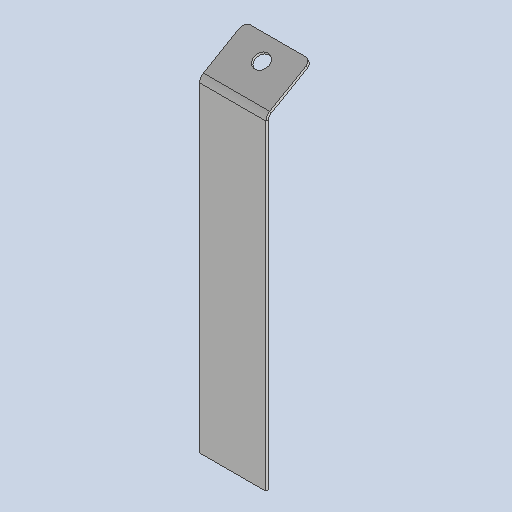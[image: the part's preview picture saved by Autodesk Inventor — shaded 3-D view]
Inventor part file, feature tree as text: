
AUTODESK INVENTOR PART (.ipt)
format: ipt  version: 2025 (Build 290162010, 162A)  size: 308,736 bytes
history: native  units: mm
features: sheet_metal_op x4, other x4, sketch x3, chamfer x1
ambient origin geometry x8: Origin, YZ Plane, XZ Plane, XY Plane, X Axis, Y Axis, Z Axis, Center Point
bodies: Solid1 (feature_tree)
feature tree (12):
  sheet_metal_op  "Face1"
  sheet_metal_op  "Flange1"
  chamfer  "Corner Round1"
  sketch  "Sketch1"  dims[d6=3.0mm]
  other  "Plate1"
  sketch  "Sketch2"  dims[d7=70.0mm]
  other  "Plate2"
  sheet_metal_op  "Bend1"
  sheet_metal_op  "Corner1"
  sketch  "Sketch3"  dims[d8=343.0mm d9=3.0mm d10=1.5mm d11=6.0mm d12=5.0mm d13=55.0mm d14=60.0deg d15=5.0mm d16=12.0mm d17=3.0mm d18=5.0mm d19=20.0mm d20=16.0mm d21=3.0mm d22=0.0mm d23=6.0mm d24=0.872665mm]
  other  "Cut1"
  other  "Definition1"
